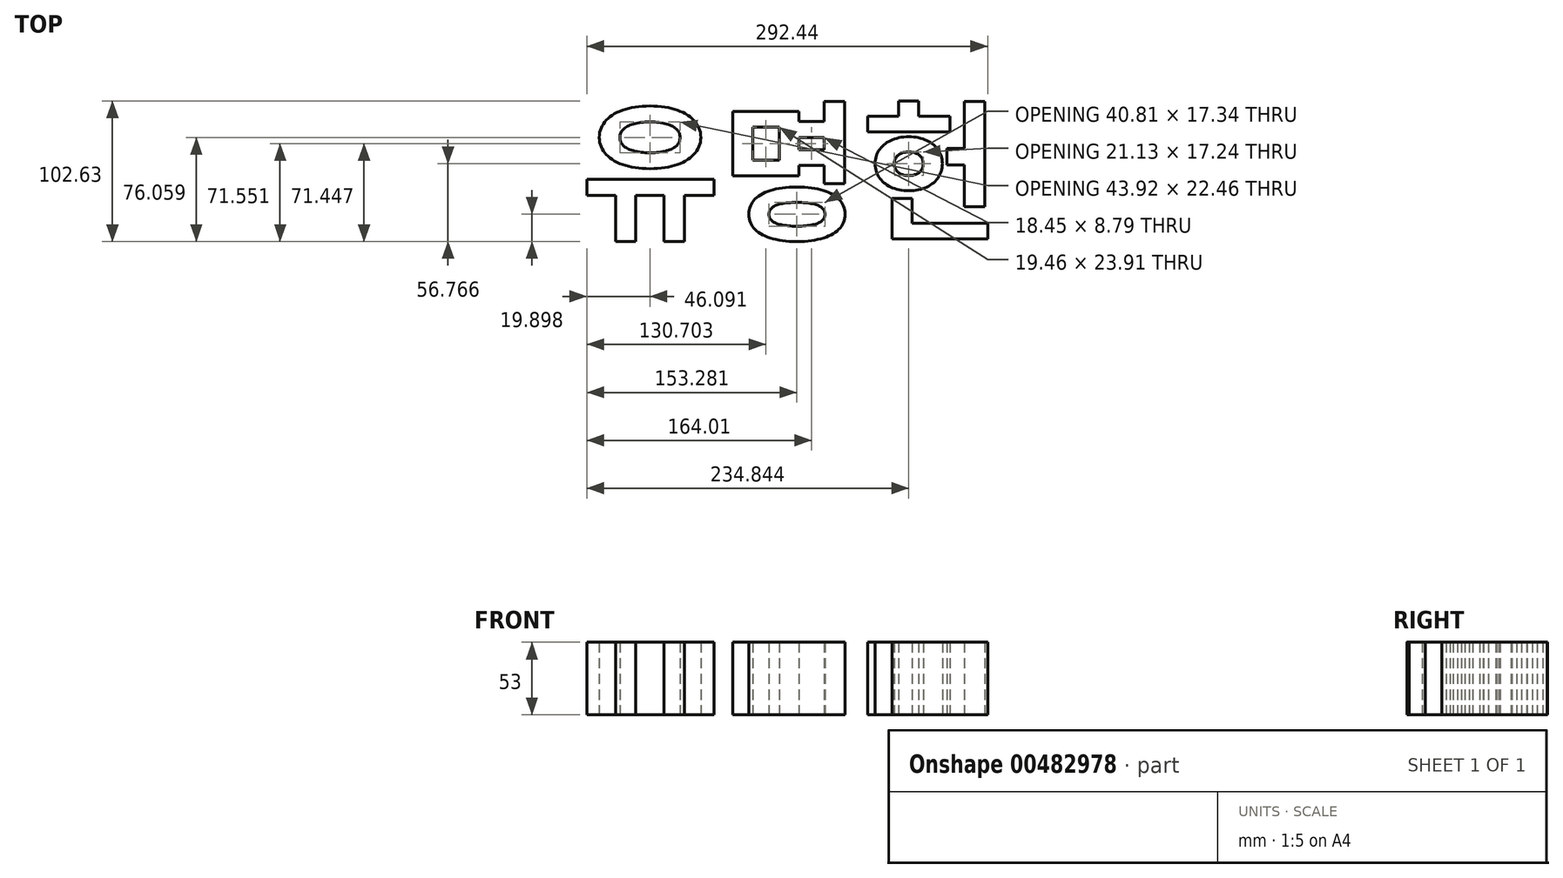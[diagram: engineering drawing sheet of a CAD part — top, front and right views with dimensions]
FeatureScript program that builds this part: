
annotation { "Feature Type Name" : "Feature", "Feature Type Description" : "" }
export const myFeature = defineFeature(function(context is Context, id is Id, definition is map)
    precondition{}
    {
        {
            var Q0;
            Q0=qCreatedBy(makeId("Top.planeOp"),FACE);
            var sketch = newSketch(context, id + "F0", { "sketchPlane" : qUnion([Q0])});
            skText(sketch, "E0", { "text": "유명헌", "fontName": "NotoSansCJKkr-Bold.otf"});
            const initialGuessF0  = {"E0": [-0.0614, -0.02911, 1, 0, 0.08006]};
            skSetInitialGuess(sketch, initialGuessF0);
            skSolve(sketch);
        }
        {
            var Q0;
            Q0 = qSketchRegion(id + "F0", true);
            extrude(context, id + "F1", {"entities" : qUnion([Q0]), "depth" : 53 * mm});
        }
    });
